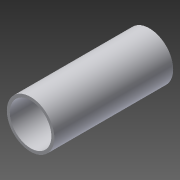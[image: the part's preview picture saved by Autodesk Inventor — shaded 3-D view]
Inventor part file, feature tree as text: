
AUTODESK INVENTOR PART (.ipt)
format: ipt  version: 2015 (Build 190159000, 159)  size: 94,208 bytes
history: native  units: mm
features: other x1, extrude x1, shell x1, sketch x1
ambient origin geometry x8: Origin, YZ Plane, XZ Plane, XY Plane, X Axis, Y Axis, Z Axis, Center Point
bodies: Body1 (feature_tree)
feature tree (4):
  other  "Bryła1"
  extrude  "Wyciągnięcie proste1"  Depth=32.0mm
  shell  "Skorupa1"  Thickness=80.0mm
  sketch  "Szkic1"
